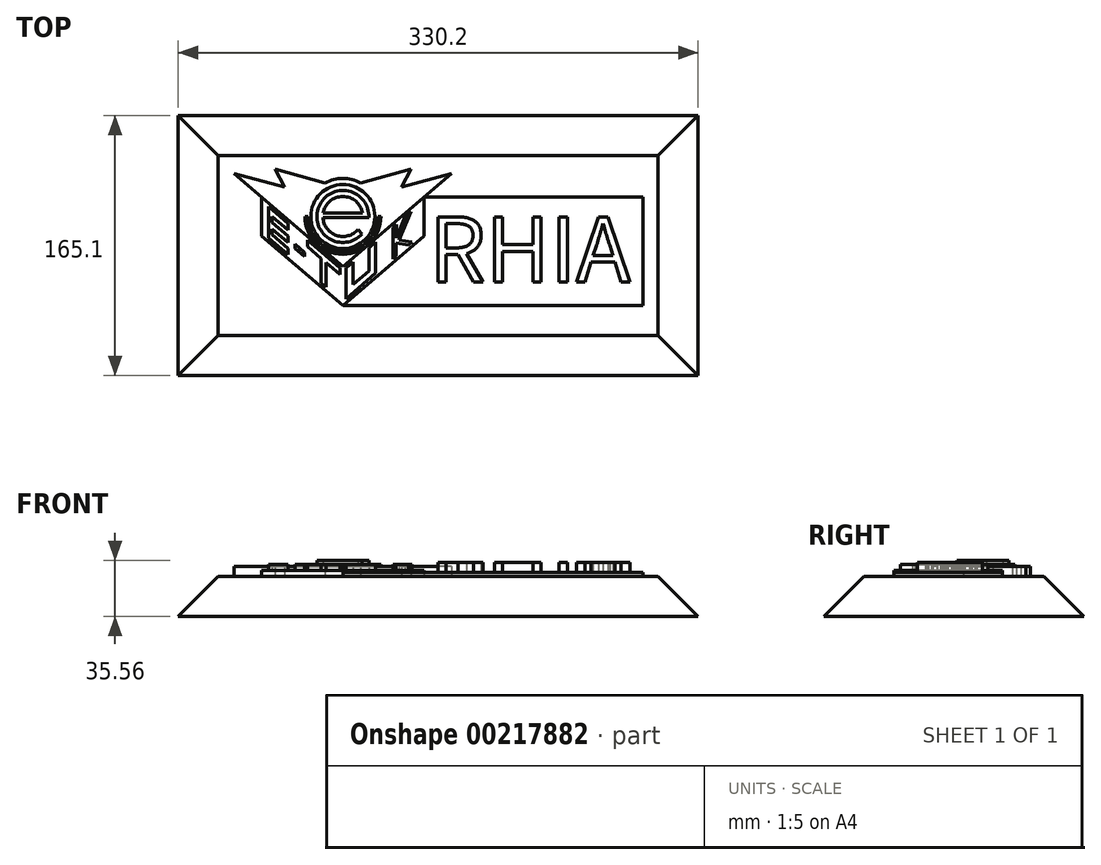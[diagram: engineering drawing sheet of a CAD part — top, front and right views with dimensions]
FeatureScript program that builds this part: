
annotation { "Feature Type Name" : "Feature", "Feature Type Description" : "" }
export const myFeature = defineFeature(function(context is Context, id is Id, definition is map)
    precondition{}
    {
        {
            var Q0;
            Q0=qCreatedBy(makeId("Top.planeOp"),FACE);
            var sketch = newSketch(context, id + "F0", { "sketchPlane" : qUnion([Q0])});
            skArc(sketch, "E0", {"start": v(12.53, 2.07) * mm, "mid": v(0, 12.7) * mm, "end": v(-12.53, 2.07) * mm});
            skArc(sketch, "E1", {"start": v(16.5, -0.78) * mm, "mid": v(-15.23, 6.37) * mm, "end": v(12.14, -11.18) * mm});
            skLineSegment(sketch, "E2", {"start": v(12.7, -0.78) * mm, "end": v(-12.68, -0.78) * mm});
            skLineSegment(sketch, "E3", {"start": v(-12.68, -0.78) * mm, "end": v(16.5, -0.78) * mm});
            skLineSegment(sketch, "E4", {"start": v(9.59, -8.33) * mm, "end": v(12.14, -11.18) * mm});
            skArc(sketch, "E5.trimOffspring", {"start": v(-12.68, -0.78) * mm, "mid": v(-4.08, -12.03) * mm, "end": v(9.59, -8.33) * mm});
            skLineSegment(sketch, "E6", {"start": v(-12.53, 2.07) * mm, "end": v(12.53, 2.07) * mm});
            skSolve(sketch);
        }
        {
            var Q0;
            Q0=makeQuery(id+"F0.imprint","IMPRINT",FACE,{"disambiguationData":[TD([[makeQuery(id+"F0.imprint","IMPRINT",EDGE,{"derivedFrom":sQuery(id+"F0.wireOp",EDGE,"E0")}),-1.0]])]});
            extrude(context, id + "F1", {"entities" : qUnion([Q0]), "depth" : 10.16 * mm});
        }
        {
            var Q0;
            Q0=qCreatedBy(makeId("Top.planeOp"),FACE);
            var sketch = newSketch(context, id + "F2", { "sketchPlane" : qUnion([Q0])});
            skCircle(sketch, "E7", {"center": v(0, 0) * mm, "radius": 20.32 * mm});
            skSolve(sketch);
        }
        {
            var Q0;
            Q0=qSketchRegion(id+"F2",true);
            extrude(context, id + "F3", {"entities" : qUnion([Q0]), "operationType" : NewBodyOperationType.ADD, "depth" : 7.62 * mm});
        }
        {
            var Q0;
            Q0=qCreatedBy(makeId("Top.planeOp"),FACE);
            var sketch = newSketch(context, id + "F4", { "sketchPlane" : qUnion([Q0])});
            skLineSegment(sketch, "E8", {"start": v(-69.02, 27.27) * mm, "end": v(-37.13, 18.72) * mm});
            skLineSegment(sketch, "E9", {"start": v(-37.13, 18.72) * mm, "end": v(-43.14, 30.14) * mm});
            skLineSegment(sketch, "E10", {"start": v(-43.14, 30.14) * mm, "end": v(-11.32, 21.31) * mm});
            skLineSegment(sketch, "E11", {"start": v(-69.02, 27.27) * mm, "end": v(0, -31.75) * mm});
            skLineSegment(sketch, "E12.MirrorCS", {"start": v(43.14, 30.14) * mm, "end": v(11.32, 21.31) * mm});
            skLineSegment(sketch, "E13.MirrorCS", {"start": v(69.02, 27.27) * mm, "end": v(0, -31.75) * mm});
            skLineSegment(sketch, "E14.MirrorCS", {"start": v(69.02, 27.27) * mm, "end": v(37.13, 18.72) * mm});
            skLineSegment(sketch, "E15.MirrorCS", {"start": v(37.13, 18.72) * mm, "end": v(43.14, 30.14) * mm});
            skArc(sketch, "E16.trimOffspring", {"start": v(11.32, 21.31) * mm, "mid": v(0, 24.13) * mm, "end": v(-11.32, 21.31) * mm});
            skSolve(sketch);
        }
        {
            var Q0;
            Q0=qSketchRegion(id+"F4",true);
            var Q1;
            Q1=makeQuery(id+"F2.imprint","IMPRINT",FACE,{"disambiguationData":[TD([[makeQuery(id+"F2.imprint","IMPRINT",EDGE,{"derivedFrom":sQuery(id+"F2.wireOp",EDGE,"E7")}),1.0]])]});
            extrude(context, id + "F5", {"entities" : qUnion([Q0, Q1]), "operationType" : NewBodyOperationType.ADD, "depth" : 6.35 * mm});
        }
        {
            var Q0;
            Q0=qCreatedBy(makeId("Top.planeOp"),FACE);
            var sketch = newSketch(context, id + "F6", { "sketchPlane" : qUnion([Q0])});
            skLineSegment(sketch, "E17", {"start": v(-51.6, -12.38) * mm, "end": v(0, -56.51) * mm});
            skLineSegment(sketch, "E18", {"start": v(0, -56.51) * mm, "end": v(51.6, -12.38) * mm});
            skLineSegment(sketch, "E19", {"start": v(-51.6, 12.38) * mm, "end": v(-51.6, -12.38) * mm});
            skLineSegment(sketch, "E20", {"start": v(51.6, 12.38) * mm, "end": v(51.6, -12.38) * mm});
            skLineSegment(sketch, "E21", {"start": v(-51.6, 12.38) * mm, "end": v(0, -31.75) * mm});
            skLineSegment(sketch, "E22", {"start": v(0, -31.75) * mm, "end": v(51.6, 12.38) * mm});
            skSolve(sketch);
        }
        {
            var Q0;
            Q0=qSketchRegion(id+"F6",true);
            extrude(context, id + "F7", {"entities" : qUnion([Q0]), "operationType" : NewBodyOperationType.ADD, "depth" : 3.8 * mm});
        }
        {
            var Q0;
            Q0=makeQuery(id+"F7.opExtrude","CAP_FACE",FACE,{"disambiguationData":[OSD([sQuery(id+"F6.wireOp",EDGE,"E17"),sQuery(id+"F6.wireOp",EDGE,"E18"),sQuery(id+"F6.wireOp",EDGE,"E19"),sQuery(id+"F6.wireOp",EDGE,"E20"),sQuery(id+"F6.wireOp",EDGE,"E21"),sQuery(id+"F6.wireOp",EDGE,"E22")])],"isStart":false});
            var sketch = newSketch(context, id + "F8", { "sketchPlane" : qUnion([Q0])});
            skPoint(sketch, "E23.startSnap0", {"position": v(-51.6, 0) * mm});
            skLineSegment(sketch, "E24", {"start": v(-51.6, -9.87) * mm, "end": v(-51.6, 9.87) * mm, "construction": true});
            skLineSegment(sketch, "E25", {"start": v(-47.26, 6.16) * mm, "end": v(-34.74, -4.55) * mm});
            skLineSegment(sketch, "E26", {"start": v(-34.74, -4.55) * mm, "end": v(-34.74, -8.63) * mm});
            skLineSegment(sketch, "E27", {"start": v(-34.74, -8.63) * mm, "end": v(-44.83, 0) * mm});
            skLineSegment(sketch, "E28", {"start": v(-44.83, 0) * mm, "end": v(-44.83, -3.75) * mm});
            skLineSegment(sketch, "E29", {"start": v(-44.83, -3.75) * mm, "end": v(-34.74, -12.38) * mm});
            skLineSegment(sketch, "E30", {"start": v(-34.74, -12.38) * mm, "end": v(-34.74, -16.46) * mm});
            skLineSegment(sketch, "E31", {"start": v(-34.74, -16.46) * mm, "end": v(-44.83, -7.83) * mm});
            skLineSegment(sketch, "E32", {"start": v(-44.83, -7.83) * mm, "end": v(-44.83, -11.58) * mm});
            skLineSegment(sketch, "E33", {"start": v(-44.83, -11.58) * mm, "end": v(-34.74, -20.21) * mm});
            skLineSegment(sketch, "E34", {"start": v(-34.74, -20.21) * mm, "end": v(-34.74, -24.3) * mm});
            skLineSegment(sketch, "E35", {"start": v(-34.74, -24.3) * mm, "end": v(-47.26, -13.59) * mm});
            skLineSegment(sketch, "E36", {"start": v(-47.26, 6.16) * mm, "end": v(-47.26, -13.59) * mm});
            skLineSegment(sketch, "E37", {"start": v(-30.38, -20.21) * mm, "end": v(-30.38, -17.65) * mm});
            skLineSegment(sketch, "E38", {"start": v(-30.38, -17.65) * mm, "end": v(-24.17, -22.96) * mm});
            skLineSegment(sketch, "E39", {"start": v(-24.17, -22.96) * mm, "end": v(-24.17, -25.53) * mm});
            skLineSegment(sketch, "E40", {"start": v(-24.17, -25.53) * mm, "end": v(-30.38, -20.21) * mm});
            skLineSegment(sketch, "E41", {"start": v(-22.38, -15.12) * mm, "end": v(-1.9, -32.63) * mm});
            skLineSegment(sketch, "E42", {"start": v(-1.9, -32.63) * mm, "end": v(-1.9, -36.71) * mm});
            skLineSegment(sketch, "E43", {"start": v(-1.9, -36.71) * mm, "end": v(-10.6, -29.28) * mm});
            skLineSegment(sketch, "E44", {"start": v(-10.6, -29.28) * mm, "end": v(-10.6, -44.95) * mm});
            skLineSegment(sketch, "E45", {"start": v(-10.6, -44.95) * mm, "end": v(-13.7, -42.3) * mm});
            skLineSegment(sketch, "E46", {"start": v(-13.7, -42.3) * mm, "end": v(-13.7, -26.63) * mm});
            skLineSegment(sketch, "E47", {"start": v(-13.7, -26.63) * mm, "end": v(-22.38, -19.2) * mm});
            skLineSegment(sketch, "E48", {"start": v(-22.38, -19.2) * mm, "end": v(-22.38, -15.12) * mm});
            skLineSegment(sketch, "E49", {"start": v(1.9, -32.62) * mm, "end": v(6.3, -28.86) * mm});
            skLineSegment(sketch, "E50", {"start": v(6.3, -28.86) * mm, "end": v(6.3, -43.26) * mm});
            skLineSegment(sketch, "E51", {"start": v(6.3, -43.26) * mm, "end": v(16.5, -34.54) * mm});
            skLineSegment(sketch, "E52", {"start": v(16.5, -34.54) * mm, "end": v(16.5, -20.14) * mm});
            skLineSegment(sketch, "E53", {"start": v(16.5, -20.14) * mm, "end": v(20.85, -16.3) * mm});
            skLineSegment(sketch, "E54", {"start": v(20.85, -16.3) * mm, "end": v(20.85, -36.06) * mm});
            skLineSegment(sketch, "E55", {"start": v(20.85, -36.06) * mm, "end": v(1.9, -52.37) * mm});
            skLineSegment(sketch, "E56", {"start": v(1.9, -52.37) * mm, "end": v(1.9, -32.62) * mm});
            skLineSegment(sketch, "E57", {"start": v(31.73, -7.12) * mm, "end": v(31.73, -27.15) * mm});
            skLineSegment(sketch, "E58", {"start": v(31.73, -27.15) * mm, "end": v(33.91, -25.22) * mm});
            skLineSegment(sketch, "E59", {"start": v(33.91, -25.22) * mm, "end": v(33.91, -16.82) * mm});
            skLineSegment(sketch, "E60", {"start": v(33.94, -13.64) * mm, "end": v(33.94, -5.23) * mm});
            skLineSegment(sketch, "E61", {"start": v(33.94, -5.23) * mm, "end": v(31.73, -7.12) * mm});
            skLineSegment(sketch, "E62", {"start": v(41.79, -18.27) * mm, "end": v(44, -16.38) * mm});
            skLineSegment(sketch, "E63", {"start": v(33.94, -13.64) * mm, "end": v(39.5, 0) * mm});
            skLineSegment(sketch, "E64", {"start": v(33.91, -16.82) * mm, "end": v(41.79, -18.27) * mm});
            skLineSegment(sketch, "E65", {"start": v(44, -16.38) * mm, "end": v(35.85, -14.87) * mm});
            skLineSegment(sketch, "E66", {"start": v(35.85, -14.87) * mm, "end": v(43.2, 3.16) * mm});
            skLineSegment(sketch, "E67", {"start": v(39.5, 0) * mm, "end": v(43.2, 3.16) * mm});
            skSolve(sketch);
        }
        {
            var Q0;
            Q0=qSketchRegion(id+"F8",true);
            extrude(context, id + "F9", {"entities" : qUnion([Q0]), "operationType" : NewBodyOperationType.ADD, "depth" : 3.8 * mm});
        }
        {
            var Q0;
            Q0=makeQuery(id+"F5.boolean.opBoolean","MERGE",FACE,{"derivedFrom":[makeQuery(id+"F5.opExtrude","CAP_FACE",FACE,{"disambiguationData":[OSD([sQuery(id+"F2.wireOp",EDGE,"E7")])],"isStart":false}),makeQuery(id+"F5.opExtrude","CAP_FACE",FACE,{"disambiguationData":[OSD([sQuery(id+"F4.wireOp",EDGE,"E8"),sQuery(id+"F4.wireOp",EDGE,"E9"),sQuery(id+"F4.wireOp",EDGE,"E10"),sQuery(id+"F4.wireOp",EDGE,"E11"),sQuery(id+"F4.wireOp",EDGE,"E13.MirrorCS"),sQuery(id+"F4.wireOp",EDGE,"E14.MirrorCS"),sQuery(id+"F4.wireOp",EDGE,"E12.MirrorCS"),sQuery(id+"F4.wireOp",EDGE,"E15.MirrorCS"),sQuery(id+"F4.wireOp",EDGE,"E16.trimOffspring")])],"isStart":false})]});
            var sketch = newSketch(context, id + "F10", { "sketchPlane" : qUnion([Q0])});
            skArc(sketch, "E68", {"start": v(-24.13, 0) * mm, "mid": v(0, -24.13) * mm, "end": v(24.13, 0) * mm});
            skArc(sketch, "E69", {"start": v(-22.23, 0) * mm, "mid": v(0, -22.23) * mm, "end": v(22.23, 0) * mm});
            skLineSegment(sketch, "E70", {"start": v(-24.13, 0) * mm, "end": v(-22.23, 0) * mm});
            skLineSegment(sketch, "E71", {"start": v(24.13, 0) * mm, "end": v(22.23, 0) * mm});
            skSolve(sketch);
        }
        {
            var Q0;
            Q0=qSketchRegion(id+"F10",true);
            extrude(context, id + "F11", {"entities" : qUnion([Q0]), "operationType" : NewBodyOperationType.ADD, "depth" : 1.27 * mm});
        }
        {
            var Q0;
            {var subQ0=sQuery(id+"F2.wireOp",EDGE,"E7");Q0=makeQuery(id+"F7.boolean.opBoolean","MERGE",FACE,{"derivedFrom":[makeQuery(id+"F5.boolean.opBoolean","MERGE",FACE,{"derivedFrom":[makeQuery(id+"F3.boolean.opBoolean","MERGE",FACE,{"derivedFrom":[makeQuery(id+"F1.opExtrude","CAP_FACE",FACE,{"disambiguationData":[OSD([sQuery(id+"F0.wireOp",EDGE,"E0"),sQuery(id+"F0.wireOp",EDGE,"E1"),sQuery(id+"F0.wireOp",EDGE,"E3"),sQuery(id+"F0.wireOp",EDGE,"E4"),sQuery(id+"F0.wireOp",EDGE,"E5.trimOffspring"),sQuery(id+"F0.wireOp",EDGE,"E6")])],"isStart":true}),makeQuery(id+"F3.opExtrude","CAP_FACE",FACE,{"disambiguationData":[OSD([subQ0])],"isStart":true})]}),makeQuery(id+"F5.opExtrude","CAP_FACE",FACE,{"disambiguationData":[OSD([subQ0])],"isStart":true}),makeQuery(id+"F5.opExtrude","CAP_FACE",FACE,{"disambiguationData":[OSD([sQuery(id+"F4.wireOp",EDGE,"E8"),sQuery(id+"F4.wireOp",EDGE,"E9"),sQuery(id+"F4.wireOp",EDGE,"E10"),sQuery(id+"F4.wireOp",EDGE,"E11"),sQuery(id+"F4.wireOp",EDGE,"E13.MirrorCS"),sQuery(id+"F4.wireOp",EDGE,"E14.MirrorCS"),sQuery(id+"F4.wireOp",EDGE,"E12.MirrorCS"),sQuery(id+"F4.wireOp",EDGE,"E15.MirrorCS"),sQuery(id+"F4.wireOp",EDGE,"E16.trimOffspring")])],"isStart":true})]}),makeQuery(id+"F7.opExtrude","CAP_FACE",FACE,{"disambiguationData":[OSD([sQuery(id+"F6.wireOp",EDGE,"E17"),sQuery(id+"F6.wireOp",EDGE,"E18"),sQuery(id+"F6.wireOp",EDGE,"E19"),sQuery(id+"F6.wireOp",EDGE,"E20"),sQuery(id+"F6.wireOp",EDGE,"E21"),sQuery(id+"F6.wireOp",EDGE,"E22")])],"isStart":true})]});}
            var sketch = newSketch(context, id + "F12", { "sketchPlane" : qUnion([Q0])});
            skLineSegment(sketch, "E72.bottom", {"start": v(0, 56.51) * mm, "end": v(190.5, 56.51) * mm});
            skLineSegment(sketch, "E72.right", {"start": v(190.5, 56.51) * mm, "end": v(190.5, -12.38) * mm});
            skLineSegment(sketch, "E73", {"start": v(51.6, -12.38) * mm, "end": v(190.5, -12.38) * mm});
            skLineSegment(sketch, "E74", {"start": v(0, 56.51) * mm, "end": v(51.6, 12.38) * mm});
            skLineSegment(sketch, "E75", {"start": v(51.6, 12.38) * mm, "end": v(51.6, -12.38) * mm});
            skSolve(sketch);
        }
        {
            var Q0;
            Q0=qSketchRegion(id+"F12",true);
            extrude(context, id + "F13", {"entities" : qUnion([Q0]), "operationType" : NewBodyOperationType.ADD, "oppositeDirection" : true, "depth" : 2.54 * mm});
        }
        {
            var Q0;
            Q0=makeQuery(id+"F13.opExtrude","CAP_FACE",FACE,{"disambiguationData":[OSD([sQuery(id+"F12.wireOp",EDGE,"E72.bottom"),sQuery(id+"F12.wireOp",EDGE,"E72.right"),sQuery(id+"F12.wireOp",EDGE,"E73"),sQuery(id+"F12.wireOp",EDGE,"E74"),sQuery(id+"F12.wireOp",EDGE,"E75")])],"isStart":false});
            var sketch = newSketch(context, id + "F14", { "sketchPlane" : qUnion([Q0])});
            skText(sketch, "E76", { "text": "RHIA", "fontName": "NotoSansCJKkr-Regular.otf"});
            const initialGuessF14  = {"E76": [0.05473, -0.0417, 1, 0, 0.04064]};
            skSetInitialGuess(sketch, initialGuessF14);
            skSolve(sketch);
        }
        {
            var Q0;
            Q0 = qSketchRegion(id + "F14", true);
            extrude(context, id + "F15", {"entities" : qUnion([Q0]), "operationType" : NewBodyOperationType.ADD, "depth" : 6.35 * mm});
        }
        {
            var Q0;
            Q0=makeQuery(id+"F13.opExtrude","CAP_FACE",FACE,{"disambiguationData":[OSD([sQuery(id+"F12.wireOp",EDGE,"E72.bottom"),sQuery(id+"F12.wireOp",EDGE,"E72.right"),sQuery(id+"F12.wireOp",EDGE,"E73"),sQuery(id+"F12.wireOp",EDGE,"E74"),sQuery(id+"F12.wireOp",EDGE,"E75")])],"isStart":true});
            var sketch = newSketch(context, id + "F16", { "sketchPlane" : qUnion([Q0])});
            skLineSegment(sketch, "E77.bottom", {"start": v(-79.18, -38.74) * mm, "end": v(200.22, -38.74) * mm});
            skLineSegment(sketch, "E77.top", {"start": v(-79.18, 75.56) * mm, "end": v(200.22, 75.56) * mm});
            skLineSegment(sketch, "E77.left", {"start": v(-79.18, -38.74) * mm, "end": v(-79.18, 75.56) * mm});
            skLineSegment(sketch, "E77.right", {"start": v(200.22, -38.74) * mm, "end": v(200.22, 75.56) * mm});
            skSolve(sketch);
        }
        {
            var Q0;
            Q0 = qSketchRegion(id + "F16", true);
            extrude(context, id + "F17", {"entities" : qUnion([Q0]), "operationType" : NewBodyOperationType.ADD, "depth" : 25.4 * mm, "hasDraft" : true, "draftAngle" : 45 * degree});
        }
    });
